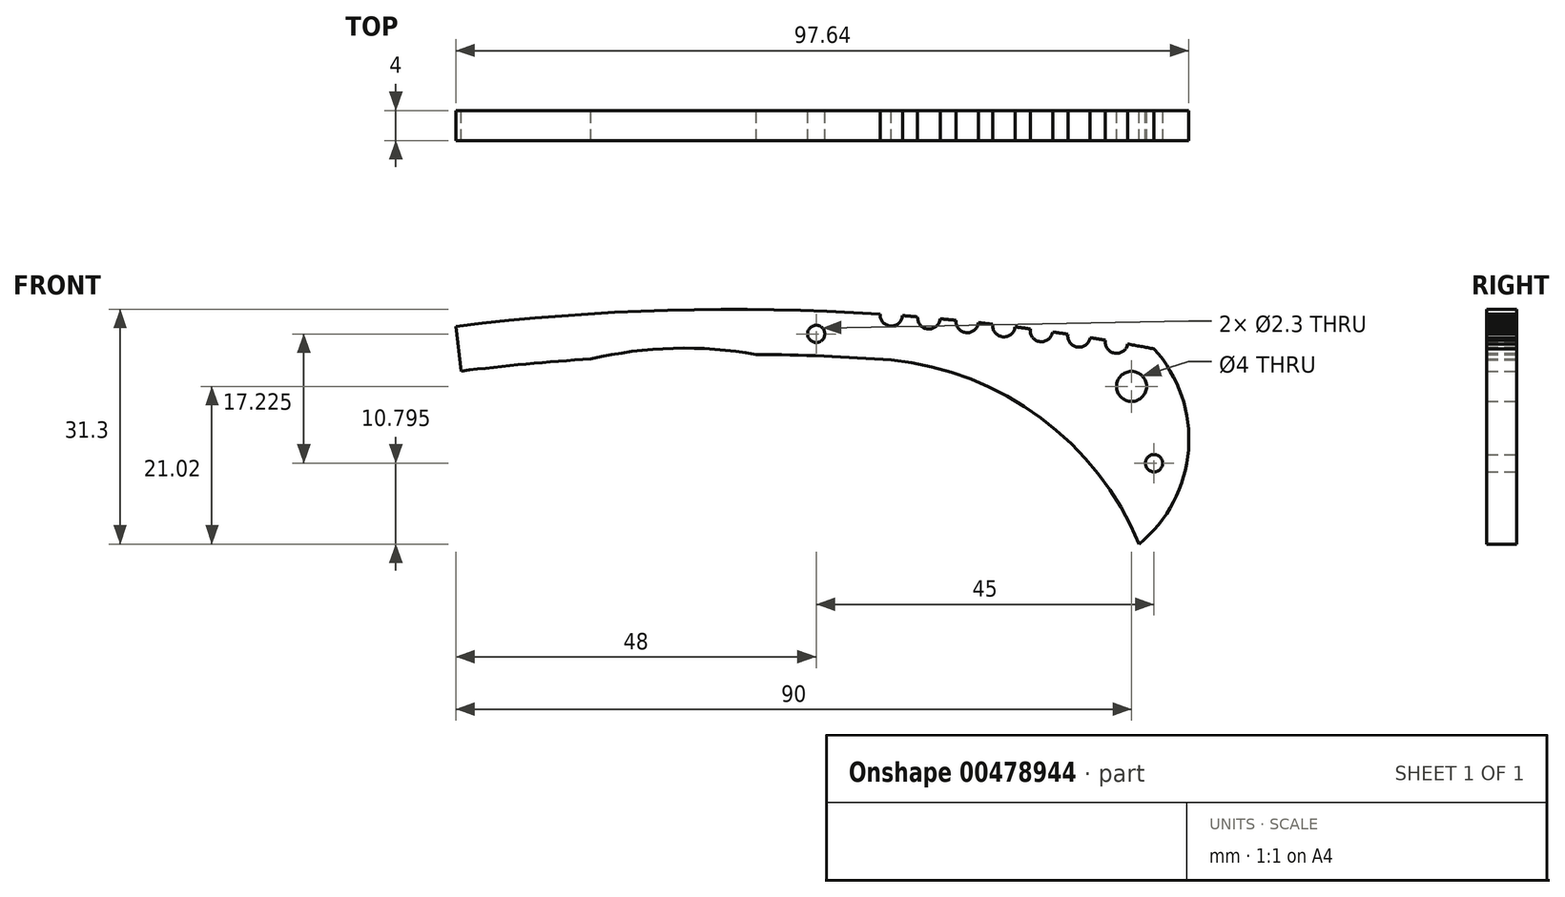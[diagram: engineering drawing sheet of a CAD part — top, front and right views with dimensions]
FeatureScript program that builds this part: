
annotation { "Feature Type Name" : "Feature", "Feature Type Description" : "" }
export const myFeature = defineFeature(function(context is Context, id is Id, definition is map)
    precondition{}
    {
        {
            var Q0;
            Q0=qCreatedBy(makeId("Front.planeOp"),FACE);
            var sketch = newSketch(context, id + "F0", { "sketchPlane" : qUnion([Q0])});
            skArc(sketch, "E0", {"start": v(85, 9) * mm, "mid": v(83.24, 9.33) * mm, "end": v(81.48, 9.65) * mm});
            skArc(sketch, "E1", {"start": v(80, -19) * mm, "mid": v(89.36, -6.22) * mm, "end": v(85, 9) * mm});
            skArc(sketch, "E2.0", {"start": v(50, 7.53) * mm, "mid": v(41, 8.04) * mm, "end": v(32, 8.27) * mm});
            skArc(sketch, "E3", {"start": v(83, -17.02) * mm, "mid": v(69.9, -0.18) * mm, "end": v(50, 7.53) * mm});
            skLineSegment(sketch, "E4", {"start": v(-8, 12) * mm, "end": v(-7.26, 6.05) * mm});
            skArc(sketch, "E5", {"start": v(48.5, 13.65) * mm, "mid": v(49.9, 12.05) * mm, "end": v(51.5, 13.43) * mm});
            skArc(sketch, "E6", {"start": v(58.6, 12.81) * mm, "mid": v(59.95, 11.17) * mm, "end": v(61.6, 12.5) * mm});
            skArc(sketch, "E7", {"start": v(53.5, 13.28) * mm, "mid": v(54.87, 11.66) * mm, "end": v(56.5, 13.02) * mm});
            skArc(sketch, "E8", {"start": v(63.51, 12.29) * mm, "mid": v(64.82, 10.62) * mm, "end": v(66.49, 11.93) * mm});
            skArc(sketch, "E9", {"start": v(68.51, 11.66) * mm, "mid": v(69.8, 9.98) * mm, "end": v(71.49, 11.25) * mm});
            skArc(sketch, "E10", {"start": v(73.52, 10.95) * mm, "mid": v(74.77, 9.25) * mm, "end": v(76.48, 10.5) * mm});
            skArc(sketch, "E11", {"start": v(78.52, 10.16) * mm, "mid": v(79.74, 8.43) * mm, "end": v(81.48, 9.65) * mm});
            skArc(sketch, "E12.trimOffspring", {"start": v(48.5, 13.65) * mm, "mid": v(20.21, 14.16) * mm, "end": v(-8, 12) * mm});
            skArc(sketch, "E13.trimOffspring", {"start": v(53.5, 13.28) * mm, "mid": v(52.5, 13.36) * mm, "end": v(51.5, 13.43) * mm});
            skArc(sketch, "E14.trimOffspring", {"start": v(58.6, 12.81) * mm, "mid": v(57.55, 12.92) * mm, "end": v(56.5, 13.02) * mm});
            skArc(sketch, "E15.trimOffspring", {"start": v(63.51, 12.29) * mm, "mid": v(62.55, 12.4) * mm, "end": v(61.6, 12.5) * mm});
            skArc(sketch, "E16.trimOffspring", {"start": v(68.51, 11.66) * mm, "mid": v(67.5, 11.8) * mm, "end": v(66.49, 11.93) * mm});
            skArc(sketch, "E17.trimOffspring", {"start": v(73.52, 10.95) * mm, "mid": v(72.5, 11.1) * mm, "end": v(71.49, 11.25) * mm});
            skArc(sketch, "E18.trimOffspring", {"start": v(78.52, 10.16) * mm, "mid": v(77.5, 10.33) * mm, "end": v(76.48, 10.5) * mm});
            skCircle(sketch, "E19", {"center": v(40, 11) * mm, "radius": 1.15 * mm});
            skArc(sketch, "E20", {"start": v(32, 8.27) * mm, "mid": v(20.97, 9.08) * mm, "end": v(10, 7.67) * mm});
            skArc(sketch, "E21.trimOffspring", {"start": v(10, 7.67) * mm, "mid": v(1.36, 6.99) * mm, "end": v(-7.26, 6.05) * mm});
            skCircle(sketch, "E22", {"center": v(82, 4) * mm, "radius": 2 * mm});
            skCircle(sketch, "E23", {"center": v(85, -6.22) * mm, "radius": 1.15 * mm});
            skSolve(sketch);
        }
        {
            var Q0;
            Q0=qSketchRegion(id+"F0",true);
            extrude(context, id + "F1", {"entities" : qUnion([Q0]), "depth" : 4 * mm});
        }
    });
